# Revit family: LAMP_LUP WALL 70 DIRECT INDIRECT
name_source: partatom
category: Luminarias
revit_build: Autodesk Revit 2018 (Build: 20190510_1515(x64)
units: mm (PartAtom-declared; Revit-internal decimal feet)

## family parameters
Anfitrión = Cara
Compartido = No
Corte con vacíos al cargar = No
Cota de conector redondo = Diámetro de uso
Origen de luz = Sí
Punto de cálculo de habitación = No
Tipo de pieza = Normal

## types (6) — shared parameters
CRI = 80
Cambio de temperatura de color de luz atenuada = <Ninguno>
Diameter = 70
Elevación por defecto = 1219 mm
Filtro de color = 16777215
Finish = Texturised black RAL 9011
Gear = Electronic
Height = 295
Installation instructions = https://www.lamp.es
Insulation class = I
Lamp = COB LED
Last update = 14/02/2022
MacAdam = 3
Manufacturer URL = http://www.lamp.es
Manufacturer country = Spain
Manufacturer name = LAMP
Material COB = LAMP_COB
Material cristal = LAMP_CRISTAL Aro Kombic
Material cuerpo = LAMP_Aluminio perfil Ocult NG
Material reflector = LAMP_Aluminio Reflector Imag
Power Supply = 220-240V 50/60Hz
Product URL = https://www.lamp.es
Product datasheet = http://www.lamp.es
Protection rating = IP65 / IK06
Weight = 1.43 kg

## per-type parameters (varying)
| type | Archivo de red fotométrica | Efficacy | Indirect light | LED Lifetime | Plum | Power | Product code | Type | Ángulo de inclinación |
| 850LM 3000 SPOT BLACK | LW170DI10SP30NB_DIR.IES | 69 lm/W | LAMP_LUP WALL 70 DIRECT INDIRECT_IND : 850LM 3000 SPOT BLACK | 50.000 L80B10 | 12 W | 11 W | LW170DI10SP30NB | COB CITIZEN | 0.00° |
| 892LM 4000 SPOT BLACK | LW170DI10SP40NB_INd.IES | 72 lm/W | LAMP_LUP WALL 70 DIRECT INDIRECT_IND : 892LM 4000 SPOT BLACK | 50.000 L80B10 | 12 W | 11 W | LW170DI10SP40NB | COB CITIZEN | 180.00° |
| 948LM 3000 MEDIUM FLOOD BLACK | LW170DI10MF30NB_ind.IES | 94 lm/W | LAMP_LUP WALL 70 DIRECT INDIRECT_IND : 948LM 3000 MEDIUM FLOOD BLACK | 50.000 L90 B10 | 10 W | 8 W | LW170DI10MF30NB | COB PHILIPS | 180.00° |
| 967LM 3000 WIDE FLOOD BLACK | LW170DI10WF30NB_ind.IES | 96 lm/W | LAMP_LUP WALL 70 DIRECT INDIRECT_IND : 967LM 3000 WIDE FLOOD BLACK | 50.000 L90 B10 | 10 W | 8 W | LW170DI10WF30NB | COB PHILIPS | 180.00° |
| 1005LM 4000 MEDIUM FLOOD BLACK | LW170DI10MF40NB_ind.IES | 100 lm/W | LAMP_LUP WALL 70 DIRECT INDIRECT_IND : 1005LM 4000 MEDIUM FLOOD BLACK | 50.000 L90 B10 | 10 W | 8 W | LW170DI10MF40NB | COB PHILIPS | 180.00° |
| 1025LM 4000 WIDE FLOOD BLACK | LW170DI10WF40NB_ind.IES | 101 lm/W | LAMP_LUP WALL 70 DIRECT INDIRECT_IND : 1025LM 4000 WIDE FLOOD BLACK | 50.000 L90 B10 | 10 W | 8 W | LW170DI10WF40NB | COB PHILIPS | 180.00° |
